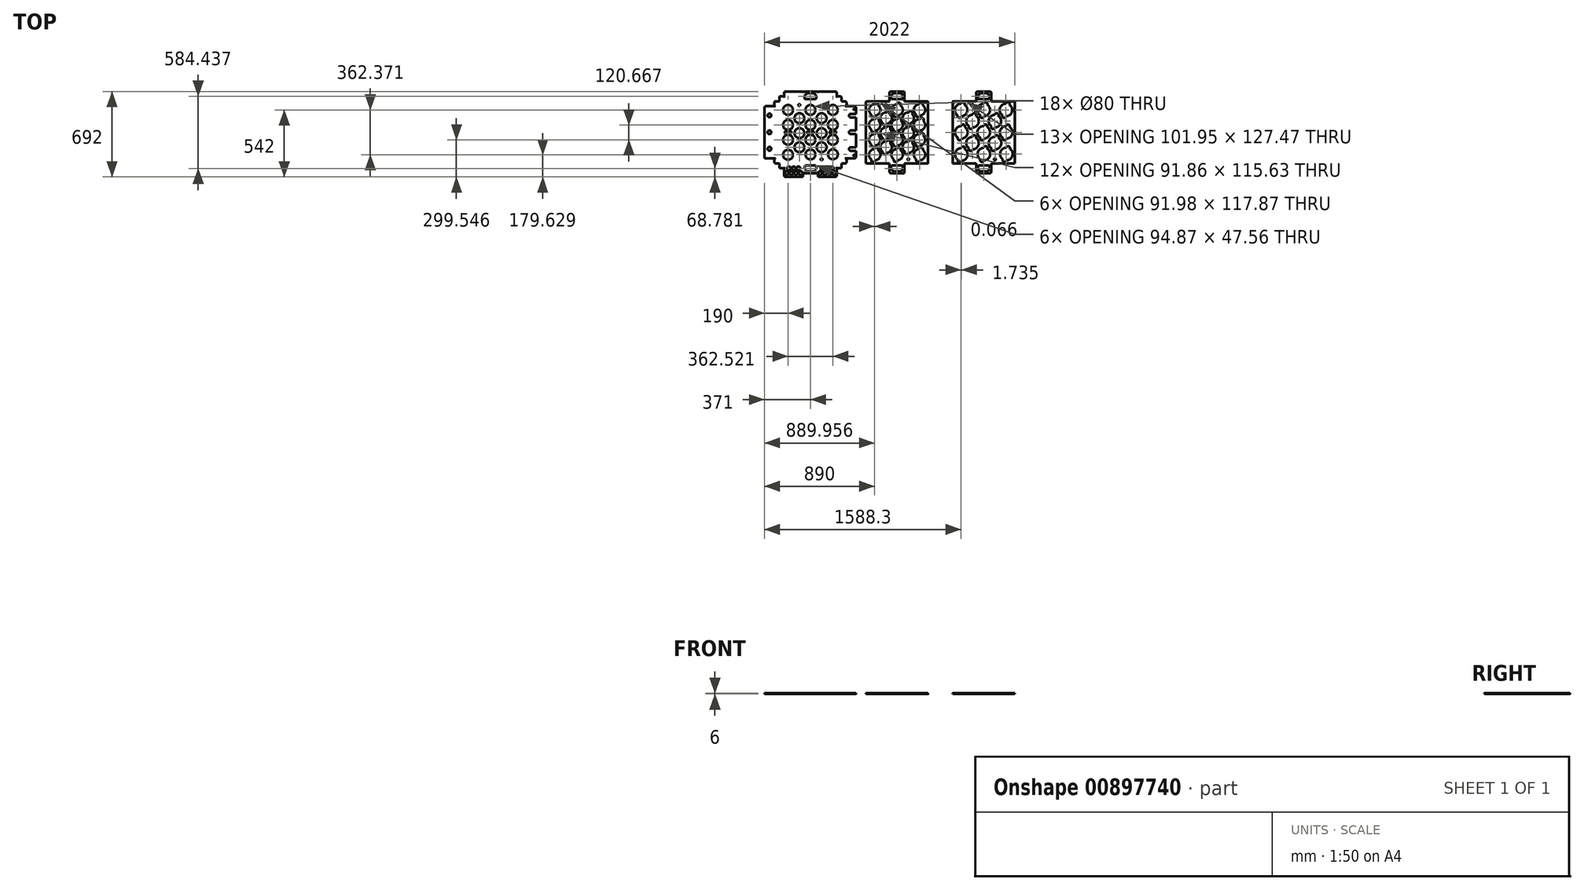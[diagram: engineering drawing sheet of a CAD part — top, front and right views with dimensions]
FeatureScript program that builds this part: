
annotation { "Feature Type Name" : "Feature", "Feature Type Description" : "" }
export const myFeature = defineFeature(function(context is Context, id is Id, definition is map)
    precondition{}
    {
        {
            var Q0;
            Q0=qCreatedBy(makeId("Top.planeOp"),FACE);
            var sketch = newSketch(context, id + "F0", { "sketchPlane" : qUnion([Q0])});
            skLineSegment(sketch, "E0", {"start": v(0, 0) * mm, "end": v(0, -30) * mm});
            skLineSegment(sketch, "E1", {"start": v(10, -40) * mm, "end": v(30, -40) * mm});
            skLineSegment(sketch, "E2", {"start": v(40, -70) * mm, "end": v(40, 0) * mm});
            skLineSegment(sketch, "E3", {"start": v(462.87, 0) * mm, "end": v(462.87, -30) * mm});
            skLineSegment(sketch, "E4", {"start": v(472.87, -40) * mm, "end": v(492, -40) * mm});
            skLineSegment(sketch, "E5", {"start": v(502, -30) * mm, "end": v(502, 0) * mm});
            skLineSegment(sketch, "E6", {"start": v(502, 0) * mm, "end": v(532, 0) * mm});
            skLineSegment(sketch, "E7", {"start": v(542, 10) * mm, "end": v(542, 30) * mm});
            skLineSegment(sketch, "E8", {"start": v(532, 40) * mm, "end": v(502, 40) * mm});
            skLineSegment(sketch, "E9", {"start": v(0, 0) * mm, "end": v(-30, 0) * mm});
            skLineSegment(sketch, "E10", {"start": v(-40, 10) * mm, "end": v(-40, 30) * mm});
            skLineSegment(sketch, "E11", {"start": v(-110, 40) * mm, "end": v(0, 40) * mm});
            skLineSegment(sketch, "E12", {"start": v(-120, 50) * mm, "end": v(-120, 251) * mm});
            skLineSegment(sketch, "E13", {"start": v(-120, 251) * mm, "end": v(45, 251) * mm, "construction": true});
            skLineSegment(sketch, "E14", {"start": v(618, 236) * mm, "end": v(618, 131) * mm});
            skLineSegment(sketch, "E15", {"start": v(251, -80) * mm, "end": v(301, -80) * mm});
            skLineSegment(sketch, "E16.MirrorCS", {"start": v(251, -80) * mm, "end": v(201, -80) * mm});
            skLineSegment(sketch, "E17.MirrorCS", {"start": v(191, -69.74) * mm, "end": v(191, 0) * mm});
            skLineSegment(sketch, "E18.0", {"start": v(298.44, -35) * mm, "end": v(298.44, -27.44) * mm});
            skLineSegment(sketch, "E18.3", {"start": v(203.56, -35) * mm, "end": v(203.56, -27.44) * mm});
            skLineSegment(sketch, "E19.0", {"start": v(213.56, -17.44) * mm, "end": v(288.44, -17.44) * mm});
            skLineSegment(sketch, "E20.0", {"start": v(268.44, -65) * mm, "end": v(233.56, -65) * mm});
            skPoint(sketch, "E21.visualSharp", {"position": v(203.56, -17.44) * mm});
            skPoint(sketch, "E22.visualSharp", {"position": v(298.44, -17.44) * mm});
            skArc(sketch, "E22.filletArc", {"start": v(298.44, -27.44) * mm, "mid": v(295.5, -20.37) * mm, "end": v(288.44, -17.44) * mm});
            skPoint(sketch, "E23.visualSharp", {"position": v(298.44, -65) * mm});
            skPoint(sketch, "E24.visualSharp", {"position": v(203.56, -65) * mm});
            skArc(sketch, "E25.filletArc", {"start": v(213.56, -17.44) * mm, "mid": v(206.5, -20.37) * mm, "end": v(203.56, -27.44) * mm});
            skPoint(sketch, "E26.visualSharp", {"position": v(311, -80) * mm});
            skArc(sketch, "E26.filletArc", {"start": v(301, -80) * mm, "mid": v(308.07, -77.07) * mm, "end": v(311, -70) * mm});
            skPoint(sketch, "E27.visualSharp", {"position": v(191, -80) * mm});
            skArc(sketch, "E27.filletArc", {"start": v(191, -70) * mm, "mid": v(193.93, -77.07) * mm, "end": v(201, -80) * mm});
            skPoint(sketch, "E28.visualSharp", {"position": v(191, 0) * mm});
            skPoint(sketch, "E29.visualSharp", {"position": v(311, 0) * mm});
            skPoint(sketch, "E30.visualSharp", {"position": v(-120, 50) * mm});
            skPoint(sketch, "E31.visualSharp", {"position": v(542, 0) * mm});
            skArc(sketch, "E31.filletArc", {"start": v(532, 0) * mm, "mid": v(539.07, 2.93) * mm, "end": v(542, 10) * mm});
            skPoint(sketch, "E32.visualSharp", {"position": v(542, 40) * mm});
            skArc(sketch, "E32.filletArc", {"start": v(542, 30) * mm, "mid": v(539.07, 37.07) * mm, "end": v(532, 40) * mm});
            skPoint(sketch, "E33.visualSharp", {"position": v(462.87, -40) * mm});
            skArc(sketch, "E33.filletArc", {"start": v(462.87, -30) * mm, "mid": v(465.8, -37.07) * mm, "end": v(472.87, -40) * mm});
            skPoint(sketch, "E34.visualSharp", {"position": v(502, -40) * mm});
            skArc(sketch, "E34.filletArc", {"start": v(492, -40) * mm, "mid": v(499.07, -37.07) * mm, "end": v(502, -30) * mm});
            skPoint(sketch, "E35.visualSharp", {"position": v(40, -40) * mm});
            skArc(sketch, "E35.filletArc", {"start": v(30, -40) * mm, "mid": v(37.07, -37.07) * mm, "end": v(40, -30) * mm});
            skPoint(sketch, "E36.visualSharp", {"position": v(0, -40) * mm});
            skArc(sketch, "E36.filletArc", {"start": v(0, -30) * mm, "mid": v(2.93, -37.07) * mm, "end": v(10, -40) * mm});
            skPoint(sketch, "E37.visualSharp", {"position": v(-40, 0) * mm});
            skArc(sketch, "E37.filletArc", {"start": v(-40, 10) * mm, "mid": v(-37.07, 2.93) * mm, "end": v(-30, 0) * mm});
            skPoint(sketch, "E38.visualSharp", {"position": v(-40, 40) * mm});
            skArc(sketch, "E38.filletArc", {"start": v(-30, 40) * mm, "mid": v(-37.07, 37.07) * mm, "end": v(-40, 30) * mm});
            skArc(sketch, "E39.MirrorCS", {"start": v(301, 582) * mm, "mid": v(308.07, 579.07) * mm, "end": v(311, 572) * mm});
            skArc(sketch, "E40.MirrorCS", {"start": v(492, 542) * mm, "mid": v(499.07, 539.07) * mm, "end": v(502, 532) * mm});
            skLineSegment(sketch, "E41.MirrorCS", {"start": v(472.87, 542) * mm, "end": v(492, 542) * mm});
            skArc(sketch, "E42.MirrorCS", {"start": v(191, 572) * mm, "mid": v(193.93, 579.07) * mm, "end": v(201, 582) * mm});
            skArc(sketch, "E43.MirrorCS", {"start": v(213.56, 519.44) * mm, "mid": v(206.5, 522.37) * mm, "end": v(203.56, 529.44) * mm});
            skArc(sketch, "E44.MirrorCS", {"start": v(542, 472) * mm, "mid": v(539.07, 464.93) * mm, "end": v(532, 462) * mm});
            skLineSegment(sketch, "E45.MirrorCS", {"start": v(203.56, 537) * mm, "end": v(203.56, 529.44) * mm});
            skArc(sketch, "E46.MirrorCS", {"start": v(462.87, 532) * mm, "mid": v(465.8, 539.07) * mm, "end": v(472.87, 542) * mm});
            skLineSegment(sketch, "E47.MirrorCS", {"start": v(-40, 492) * mm, "end": v(-40, 472) * mm});
            skLineSegment(sketch, "E48.MirrorCS", {"start": v(542, 492) * mm, "end": v(542, 472) * mm});
            skLineSegment(sketch, "E49.MirrorCS", {"start": v(298.44, 537) * mm, "end": v(298.44, 529.44) * mm});
            skLineSegment(sketch, "E50.MirrorCS", {"start": v(311, 552) * mm, "end": v(311, 502) * mm});
            skArc(sketch, "E51.MirrorCS", {"start": v(-40, 492) * mm, "mid": v(-37.07, 499.07) * mm, "end": v(-30, 502) * mm});
            skArc(sketch, "E52.MirrorCS", {"start": v(0, 532) * mm, "mid": v(2.93, 539.07) * mm, "end": v(10, 542) * mm});
            skLineSegment(sketch, "E53.MirrorCS", {"start": v(502, 502) * mm, "end": v(532, 502) * mm});
            skLineSegment(sketch, "E54.MirrorCS", {"start": v(10, 542) * mm, "end": v(30, 542) * mm});
            skArc(sketch, "E55.MirrorCS", {"start": v(298.44, 529.44) * mm, "mid": v(295.5, 522.37) * mm, "end": v(288.44, 519.44) * mm});
            skLineSegment(sketch, "E56.MirrorCS", {"start": v(-30, 462) * mm, "end": v(0, 462) * mm});
            skArc(sketch, "E57.MirrorCS", {"start": v(30, 542) * mm, "mid": v(37.07, 539.07) * mm, "end": v(40, 532) * mm});
            skArc(sketch, "E58.MirrorCS", {"start": v(532, 502) * mm, "mid": v(539.07, 499.07) * mm, "end": v(542, 492) * mm});
            skArc(sketch, "E59.MirrorCS", {"start": v(-30, 462) * mm, "mid": v(-37.07, 464.93) * mm, "end": v(-40, 472) * mm});
            skLineSegment(sketch, "E60.MirrorCS", {"start": v(532, 462) * mm, "end": v(502, 462) * mm});
            skLineSegment(sketch, "E61.MirrorCS", {"start": v(268.44, 567) * mm, "end": v(233.56, 567) * mm});
            skLineSegment(sketch, "E62.MirrorCS", {"start": v(462.87, 502) * mm, "end": v(462.87, 532) * mm});
            skLineSegment(sketch, "E63.MirrorCS", {"start": v(502, 532) * mm, "end": v(502, 502) * mm});
            skLineSegment(sketch, "E64.MirrorCS", {"start": v(0, 502) * mm, "end": v(-30, 502) * mm});
            skLineSegment(sketch, "E65.MirrorCS", {"start": v(251, 582) * mm, "end": v(201, 582) * mm});
            skLineSegment(sketch, "E66.MirrorCS", {"start": v(0, 502) * mm, "end": v(0, 532) * mm});
            skLineSegment(sketch, "E67.MirrorCS", {"start": v(40, 532) * mm, "end": v(40, 502) * mm});
            skLineSegment(sketch, "E68.MirrorCS", {"start": v(251, 582) * mm, "end": v(301, 582) * mm});
            skLineSegment(sketch, "E69.MirrorCS", {"start": v(213.56, 519.44) * mm, "end": v(288.44, 519.44) * mm});
            skPoint(sketch, "E70.MirrorP", {"position": v(203.56, 519.44) * mm});
            skPoint(sketch, "E71.MirrorP", {"position": v(0, 542) * mm});
            skPoint(sketch, "E72.MirrorP", {"position": v(40, 542) * mm});
            skPoint(sketch, "E73.MirrorP", {"position": v(542, 502) * mm});
            skPoint(sketch, "E74.MirrorP", {"position": v(298.44, 519.44) * mm});
            skPoint(sketch, "E75.MirrorP", {"position": v(311, 582) * mm});
            skPoint(sketch, "E76.MirrorP", {"position": v(502, 542) * mm});
            skPoint(sketch, "E77.MirrorP", {"position": v(191, 582) * mm});
            skPoint(sketch, "E78.MirrorP", {"position": v(462.87, 542) * mm});
            skPoint(sketch, "E79.MirrorP", {"position": v(-40, 462) * mm});
            skLineSegment(sketch, "E80.MirrorCS", {"start": v(-120, 452) * mm, "end": v(-120, 251) * mm});
            skPoint(sketch, "E81.MirrorP", {"position": v(-40, 502) * mm});
            skPoint(sketch, "E82.MirrorP", {"position": v(618, 452) * mm});
            skLineSegment(sketch, "E83.MirrorCS", {"start": v(618, 266) * mm, "end": v(618, 371) * mm});
            skLineSegment(sketch, "E84.0", {"start": v(-80, 442) * mm, "end": v(-80, 62.82) * mm, "construction": true});
            skLineSegment(sketch, "E85.0", {"start": v(578, 60.47) * mm, "end": v(578, 442) * mm, "construction": true});
            skCircle(sketch, "E86", {"center": v(-80, 251) * mm, "radius": 15 * mm});
            skPoint(sketch, "E86.centerSnap0", {"position": v(-80, 252.4) * mm});
            skArc(sketch, "E87", {"start": v(578, 266) * mm, "mid": v(563, 251) * mm, "end": v(578, 236) * mm});
            skArc(sketch, "E88", {"start": v(578, 401) * mm, "mid": v(563, 386) * mm, "end": v(578, 371) * mm});
            skArc(sketch, "E89", {"start": v(578, 131) * mm, "mid": v(563, 116) * mm, "end": v(578, 101) * mm});
            skCircle(sketch, "E90", {"center": v(-80, 387.4) * mm, "radius": 15 * mm});
            skCircle(sketch, "E91", {"center": v(-80, 117.4) * mm, "radius": 15 * mm});
            skLineSegment(sketch, "E92", {"start": v(578, 401) * mm, "end": v(618, 401) * mm});
            skLineSegment(sketch, "E93", {"start": v(578, 371) * mm, "end": v(618, 371) * mm});
            skLineSegment(sketch, "E94", {"start": v(578, 266) * mm, "end": v(618, 266) * mm});
            skLineSegment(sketch, "E95", {"start": v(578, 236) * mm, "end": v(618, 236) * mm});
            skLineSegment(sketch, "E96", {"start": v(578, 131) * mm, "end": v(618, 131) * mm});
            skLineSegment(sketch, "E97", {"start": v(578, 101) * mm, "end": v(618, 101) * mm});
            skLineSegment(sketch, "E98.trimOffspring", {"start": v(618, 401) * mm, "end": v(618, 452) * mm});
            skPoint(sketch, "E99.orphan", {"position": v(618, 251) * mm});
            skLineSegment(sketch, "E100.trimOffspring", {"start": v(618, 101) * mm, "end": v(618, 50) * mm});
            skLineSegment(sketch, "E101", {"start": v(50, 582) * mm, "end": v(181, 582) * mm});
            skPoint(sketch, "E102.visualSharp", {"position": v(170, 582) * mm});
            skLineSegment(sketch, "E103", {"start": v(452.87, 582) * mm, "end": v(321, 582) * mm});
            skLineSegment(sketch, "E104", {"start": v(191, 572) * mm, "end": v(191, 502) * mm});
            skLineSegment(sketch, "E105.0", {"start": v(432, 432) * mm, "end": v(69.97, 432) * mm, "construction": true});
            skLineSegment(sketch, "E106.0", {"start": v(432, 432) * mm, "end": v(70, 432) * mm, "construction": true});
            skLineSegment(sketch, "E107", {"start": v(70, 65) * mm, "end": v(70, 432) * mm, "construction": true});
            skLineSegment(sketch, "E108.0", {"start": v(432, 311.33) * mm, "end": v(70, 311.33) * mm, "construction": true});
            skLineSegment(sketch, "E109.0", {"start": v(432, 190.67) * mm, "end": v(70, 190.67) * mm, "construction": true});
            skLineSegment(sketch, "E110", {"start": v(251, 432) * mm, "end": v(251, 70) * mm, "construction": true});
            skCircle(sketch, "E111", {"center": v(70, 432) * mm, "radius": 40 * mm});
            skCircle(sketch, "E112", {"center": v(251, 432) * mm, "radius": 40 * mm});
            skCircle(sketch, "E113", {"center": v(432, 432) * mm, "radius": 40 * mm});
            skCircle(sketch, "E114", {"center": v(341.53, 365.69) * mm, "radius": 40 * mm});
            skCircle(sketch, "E115", {"center": v(70.07, 69.63) * mm, "radius": 40 * mm});
            skCircle(sketch, "E116", {"center": v(251, 72.13) * mm, "radius": 40 * mm});
            skCircle(sketch, "E117", {"center": v(341.53, 245.02) * mm, "radius": 40 * mm});
            skCircle(sketch, "E118", {"center": v(341.5, 130.33) * mm, "radius": 40 * mm});
            skCircle(sketch, "E119", {"center": v(432.52, 72.87) * mm, "radius": 40 * mm});
            skLineSegment(sketch, "E120", {"start": v(251, 65) * mm, "end": v(251, 427) * mm, "construction": true});
            skLineSegment(sketch, "E121.trimOffspring", {"start": v(95, 246) * mm, "end": v(95, 256) * mm});
            skLineSegment(sketch, "E122.trimOffspring", {"start": v(226, 246) * mm, "end": v(226, 256) * mm});
            skLineSegment(sketch, "E123.trimOffspring", {"start": v(276, 246) * mm, "end": v(276, 256) * mm});
            skLineSegment(sketch, "E124.trimOffspring", {"start": v(457.52, 246) * mm, "end": v(457.52, 256) * mm});
            skLineSegment(sketch, "E125.trimOffspring", {"start": v(407.52, 246) * mm, "end": v(407.52, 256) * mm});
            skArc(sketch, "E126.trimOffspring", {"start": v(432.52, 230.66) * mm, "mid": v(432.26, 230.67) * mm, "end": v(432, 230.67) * mm});
            skArc(sketch, "E127.trimOffspring", {"start": v(432, 271.33) * mm, "mid": v(432.26, 271.33) * mm, "end": v(432.52, 271.34) * mm});
            skLineSegment(sketch, "E128", {"start": v(70.07, 69.63) * mm, "end": v(70.02, 230.67) * mm, "construction": true});
            skLineSegment(sketch, "E129", {"start": v(432, 432) * mm, "end": v(432.52, 70.74) * mm, "construction": true});
            skLineSegment(sketch, "E130", {"start": v(341.5, 130.33) * mm, "end": v(341.53, 365.69) * mm, "construction": true});
            skLineSegment(sketch, "E131", {"start": v(69.99, 365.69) * mm, "end": v(251, 365.69) * mm, "construction": true});
            skLineSegment(sketch, "E132", {"start": v(162.1, 130.33) * mm, "end": v(162.13, 365.69) * mm, "construction": true});
            skCircle(sketch, "E133", {"center": v(162.13, 365.69) * mm, "radius": 40 * mm});
            skCircle(sketch, "E134", {"center": v(162.13, 245.02) * mm, "radius": 40 * mm});
            skCircle(sketch, "E135", {"center": v(162.1, 130.33) * mm, "radius": 40 * mm});
            skCircle(sketch, "E136.converted", {"center": v(432, 311.33) * mm, "radius": 40 * mm});
            skCircle(sketch, "E137.converted", {"center": v(251, 311.33) * mm, "radius": 40 * mm});
            skCircle(sketch, "E138.converted", {"center": v(70, 190.67) * mm, "radius": 40 * mm});
            skCircle(sketch, "E139.converted", {"center": v(251, 190.67) * mm, "radius": 40 * mm});
            skCircle(sketch, "E140.converted", {"center": v(432, 190.67) * mm, "radius": 40 * mm});
            skLineSegment(sketch, "E141", {"start": v(90, 261) * mm, "end": v(50, 261) * mm});
            skLineSegment(sketch, "E142", {"start": v(45, 256) * mm, "end": v(45, 246) * mm});
            skLineSegment(sketch, "E143", {"start": v(50, 241) * mm, "end": v(90, 241) * mm});
            skCircle(sketch, "E144.converted", {"center": v(70, 311.33) * mm, "radius": 40 * mm});
            skPoint(sketch, "E145.orphan", {"position": v(95, 280.1) * mm});
            skPoint(sketch, "E146.orphan", {"position": v(95, 221.9) * mm});
            skPoint(sketch, "E147.orphan", {"position": v(45, 221.9) * mm});
            skPoint(sketch, "E148.orphan", {"position": v(45, 280.1) * mm});
            skLineSegment(sketch, "E149.trimOffspring", {"start": v(95, 251) * mm, "end": v(563, 251) * mm, "construction": true});
            skLineSegment(sketch, "E150.trimOffspring", {"start": v(70, 251) * mm, "end": v(70.02, 251) * mm});
            skArc(sketch, "E151.filletArc", {"start": v(95, 256) * mm, "mid": v(93.54, 259.54) * mm, "end": v(90, 261) * mm});
            skArc(sketch, "E152.filletArc", {"start": v(90, 241) * mm, "mid": v(93.54, 242.46) * mm, "end": v(95, 246) * mm});
            skArc(sketch, "E153.filletArc", {"start": v(50, 261) * mm, "mid": v(46.46, 259.54) * mm, "end": v(45, 256) * mm});
            skArc(sketch, "E154.filletArc", {"start": v(45, 246) * mm, "mid": v(46.46, 242.46) * mm, "end": v(50, 241) * mm});
            skLineSegment(sketch, "E155", {"start": v(271, 261) * mm, "end": v(231, 261) * mm});
            skLineSegment(sketch, "E156", {"start": v(226, 256) * mm, "end": v(226, 246) * mm});
            skLineSegment(sketch, "E157", {"start": v(231, 241) * mm, "end": v(271, 241) * mm});
            skLineSegment(sketch, "E158.trimOffspring", {"start": v(251, 251) * mm, "end": v(251.02, 251) * mm});
            skArc(sketch, "E159.filletArc", {"start": v(276, 256) * mm, "mid": v(274.54, 259.54) * mm, "end": v(271, 261) * mm});
            skArc(sketch, "E160.filletArc", {"start": v(271, 241) * mm, "mid": v(274.54, 242.46) * mm, "end": v(276, 246) * mm});
            skArc(sketch, "E161.filletArc", {"start": v(231, 261) * mm, "mid": v(227.46, 259.54) * mm, "end": v(226, 256) * mm});
            skArc(sketch, "E162.filletArc", {"start": v(226, 246) * mm, "mid": v(227.46, 242.46) * mm, "end": v(231, 241) * mm});
            skLineSegment(sketch, "E163", {"start": v(452.52, 261) * mm, "end": v(412.52, 261) * mm});
            skLineSegment(sketch, "E164", {"start": v(407.52, 256) * mm, "end": v(407.52, 246) * mm});
            skLineSegment(sketch, "E165", {"start": v(412.52, 241) * mm, "end": v(452.52, 241) * mm});
            skLineSegment(sketch, "E166.trimOffspring", {"start": v(432.52, 251) * mm, "end": v(432.54, 251) * mm});
            skArc(sketch, "E167.filletArc", {"start": v(457.52, 256) * mm, "mid": v(456.06, 259.54) * mm, "end": v(452.52, 261) * mm});
            skArc(sketch, "E168.filletArc", {"start": v(452.52, 241) * mm, "mid": v(456.06, 242.46) * mm, "end": v(457.52, 246) * mm});
            skArc(sketch, "E169.filletArc", {"start": v(412.52, 261) * mm, "mid": v(408.99, 259.54) * mm, "end": v(407.52, 256) * mm});
            skArc(sketch, "E170.filletArc", {"start": v(407.52, 246) * mm, "mid": v(408.99, 242.46) * mm, "end": v(412.52, 241) * mm});
            skCircle(sketch, "E171", {"center": v(578, 116) * mm, "radius": 15 * mm, "construction": true});
            skLineSegment(sketch, "E172.0", {"start": v(603, 101) * mm, "end": v(603, 50) * mm, "construction": true});
            skCircle(sketch, "E173", {"center": v(603, 65) * mm, "radius": 4.25 * mm});
            skLineSegment(sketch, "E174.0", {"start": v(603, 401) * mm, "end": v(603, 452) * mm, "construction": true});
            skCircle(sketch, "E175", {"center": v(603, 437) * mm, "radius": 4.25 * mm});
            skLineSegment(sketch, "E176", {"start": v(64, 0) * mm, "end": v(164, 0) * mm, "construction": true});
            skLineSegment(sketch, "E177.0", {"start": v(77.75, -40) * mm, "end": v(115.5, -40) * mm, "construction": true});
            skCircle(sketch, "E178", {"center": v(77.75, -40) * mm, "radius": 15 * mm});
            skCircle(sketch, "E179", {"center": v(115.5, -40) * mm, "radius": 15 * mm});
            skCircle(sketch, "E180", {"center": v(153.25, -40) * mm, "radius": 15 * mm});
            skPoint(sketch, "E181.orphan", {"position": v(40, -20) * mm});
            skLineSegment(sketch, "E182", {"start": v(115.5, -40) * mm, "end": v(130.5, -40) * mm, "construction": true});
            skLineSegment(sketch, "E183", {"start": v(77.75, -40) * mm, "end": v(40, -40) * mm, "construction": true});
            skLineSegment(sketch, "E184.0", {"start": v(191, -77.75) * mm, "end": v(40, -77.75) * mm, "construction": true});
            skLineSegment(sketch, "E185", {"start": v(58.87, -40) * mm, "end": v(58.87, -77.75) * mm, "construction": true});
            skLineSegment(sketch, "E186", {"start": v(96.62, -40) * mm, "end": v(96.62, -77.75) * mm, "construction": true});
            skLineSegment(sketch, "E187", {"start": v(153.25, -40) * mm, "end": v(191, -40) * mm, "construction": true});
            skLineSegment(sketch, "E188", {"start": v(172.12, -40) * mm, "end": v(172.12, -77.75) * mm, "construction": true});
            skCircle(sketch, "E189", {"center": v(58.87, -77.75) * mm, "radius": 15 * mm});
            skCircle(sketch, "E190", {"center": v(96.62, -77.75) * mm, "radius": 15 * mm});
            skLineSegment(sketch, "E191", {"start": v(134.37, -40) * mm, "end": v(134.37, -77.75) * mm, "construction": true});
            skCircle(sketch, "E192", {"center": v(134.37, -77.75) * mm, "radius": 15 * mm});
            skCircle(sketch, "E193", {"center": v(172.12, -77.75) * mm, "radius": 15 * mm});
            skPoint(sketch, "E194.visualSharp", {"position": v(462, -80) * mm});
            skPoint(sketch, "E195.visualSharp", {"position": v(462, 0) * mm});
            skLineSegment(sketch, "E196.0", {"start": v(348.75, -40) * mm, "end": v(386.5, -40) * mm, "construction": true});
            skCircle(sketch, "E197", {"center": v(348.75, -40) * mm, "radius": 15 * mm});
            skCircle(sketch, "E198", {"center": v(386.5, -40) * mm, "radius": 15 * mm});
            skCircle(sketch, "E199", {"center": v(424.25, -40) * mm, "radius": 15 * mm});
            skLineSegment(sketch, "E200.trimOffspring", {"start": v(401.5, -40) * mm, "end": v(409.25, -40) * mm, "construction": true});
            skLineSegment(sketch, "E201", {"start": v(386.5, -40) * mm, "end": v(401.5, -40) * mm, "construction": true});
            skLineSegment(sketch, "E202", {"start": v(348.75, -40) * mm, "end": v(311, -40) * mm, "construction": true});
            skLineSegment(sketch, "E203.0", {"start": v(462, -77.75) * mm, "end": v(311, -77.75) * mm, "construction": true});
            skLineSegment(sketch, "E204", {"start": v(329.87, -40) * mm, "end": v(329.87, -77.75) * mm, "construction": true});
            skLineSegment(sketch, "E205", {"start": v(367.62, -40) * mm, "end": v(367.62, -77.75) * mm, "construction": true});
            skLineSegment(sketch, "E206", {"start": v(424.25, -40) * mm, "end": v(462, -40) * mm, "construction": true});
            skLineSegment(sketch, "E207", {"start": v(443.12, -40) * mm, "end": v(443.12, -77.75) * mm, "construction": true});
            skCircle(sketch, "E208", {"center": v(329.87, -77.75) * mm, "radius": 15 * mm});
            skCircle(sketch, "E209", {"center": v(367.62, -77.75) * mm, "radius": 15 * mm});
            skLineSegment(sketch, "E210", {"start": v(405.37, -40) * mm, "end": v(405.37, -77.75) * mm, "construction": true});
            skCircle(sketch, "E211", {"center": v(405.37, -77.75) * mm, "radius": 15 * mm});
            skCircle(sketch, "E212", {"center": v(443.12, -77.75) * mm, "radius": 15 * mm});
            skLineSegment(sketch, "E213", {"start": v(191, -69.74) * mm, "end": v(191, -70) * mm});
            skPoint(sketch, "E214.visualSharp", {"position": v(40, -80) * mm});
            skLineSegment(sketch, "E215.0", {"start": v(181, -110) * mm, "end": v(50, -110) * mm});
            skLineSegment(sketch, "E216.0", {"start": v(452.89, -109.73) * mm, "end": v(321.02, -109.98) * mm});
            skPoint(sketch, "E217.newPointA", {"position": v(203.56, -55) * mm});
            skPoint(sketch, "E217.newPointB", {"position": v(213.56, -65) * mm});
            skArc(sketch, "E217.filletArc", {"start": v(203.56, -35) * mm, "mid": v(212.35, -56.21) * mm, "end": v(233.56, -65) * mm});
            skPoint(sketch, "E218.newPointA", {"position": v(288.44, -65) * mm});
            skPoint(sketch, "E218.newPointB", {"position": v(298.44, -55) * mm});
            skArc(sketch, "E218.filletArc", {"start": v(268.44, -65) * mm, "mid": v(289.65, -56.21) * mm, "end": v(298.44, -35) * mm});
            skLineSegment(sketch, "E219", {"start": v(462.87, -30) * mm, "end": v(462.87, -99.73) * mm});
            skLineSegment(sketch, "E220", {"start": v(311, 0) * mm, "end": v(311, -99.98) * mm});
            skLineSegment(sketch, "E221", {"start": v(191, -69.74) * mm, "end": v(191, -100) * mm});
            skLineSegment(sketch, "E222", {"start": v(40, -70) * mm, "end": v(40, -100) * mm});
            skArc(sketch, "E223.filletArc", {"start": v(452.89, -109.73) * mm, "mid": v(459.95, -106.8) * mm, "end": v(462.87, -99.73) * mm});
            skPoint(sketch, "E224.visualSharp", {"position": v(311, -110) * mm});
            skArc(sketch, "E224.filletArc", {"start": v(311, -99.98) * mm, "mid": v(313.94, -107.06) * mm, "end": v(321.02, -109.98) * mm});
            skArc(sketch, "E225.filletArc", {"start": v(181, -110) * mm, "mid": v(188.07, -107.07) * mm, "end": v(191, -100) * mm});
            skArc(sketch, "E226.filletArc", {"start": v(40, -100) * mm, "mid": v(42.93, -107.07) * mm, "end": v(50, -110) * mm});
            skArc(sketch, "E227.filletArc", {"start": v(233.56, 567) * mm, "mid": v(212.35, 558.21) * mm, "end": v(203.56, 537) * mm});
            skArc(sketch, "E228.filletArc", {"start": v(298.44, 537) * mm, "mid": v(289.65, 558.21) * mm, "end": v(268.44, 567) * mm});
            skPoint(sketch, "E229.newPointA", {"position": v(311, 572) * mm});
            skLineSegment(sketch, "E230", {"start": v(311, 552) * mm, "end": v(311, 572) * mm});
            skArc(sketch, "E231.filletArc", {"start": v(321, 582) * mm, "mid": v(313.93, 579.07) * mm, "end": v(311, 572) * mm});
            skArc(sketch, "E232.filletArc", {"start": v(191, 572) * mm, "mid": v(188.07, 579.07) * mm, "end": v(181, 582) * mm});
            skLineSegment(sketch, "E233", {"start": v(70, 472) * mm, "end": v(251, 472) * mm, "construction": true});
            skCircle(sketch, "E234", {"center": v(160.5, 472) * mm, "radius": 7.5 * mm});
            skLineSegment(sketch, "E235", {"start": v(432, 32.87) * mm, "end": v(251, 32.13) * mm, "construction": true});
            skCircle(sketch, "E236", {"center": v(341.5, 32.5) * mm, "radius": 7.5 * mm});
            skPoint(sketch, "E237.orphan", {"position": v(-120, 60) * mm});
            skArc(sketch, "E238.filletArc", {"start": v(-120, 50) * mm, "mid": v(-117.07, 42.93) * mm, "end": v(-110, 40) * mm});
            skPoint(sketch, "E239.end.orphan", {"position": v(0, 50) * mm});
            skLineSegment(sketch, "E240", {"start": v(-30, 462) * mm, "end": v(-110, 462) * mm});
            skPoint(sketch, "E241.orphan", {"position": v(-120, 442) * mm});
            skArc(sketch, "E242.filletArc", {"start": v(-110, 462) * mm, "mid": v(-117.07, 459.07) * mm, "end": v(-120, 452) * mm});
            skLineSegment(sketch, "E243", {"start": v(40, 532) * mm, "end": v(40, 572) * mm});
            skPoint(sketch, "E244.orphan", {"position": v(70, 582) * mm});
            skPoint(sketch, "E245.visualSharp", {"position": v(40, 582) * mm});
            skArc(sketch, "E245.filletArc", {"start": v(50, 582) * mm, "mid": v(42.93, 579.07) * mm, "end": v(40, 572) * mm});
            skLineSegment(sketch, "E246", {"start": v(462.87, 532) * mm, "end": v(462.87, 572) * mm});
            skPoint(sketch, "E247.orphan", {"position": v(432.87, 582) * mm});
            skPoint(sketch, "E248.visualSharp", {"position": v(462.87, 582) * mm});
            skArc(sketch, "E248.filletArc", {"start": v(462.87, 572) * mm, "mid": v(459.94, 579.07) * mm, "end": v(452.87, 582) * mm});
            skLineSegment(sketch, "E249", {"start": v(532, 462) * mm, "end": v(608, 462) * mm});
            skPoint(sketch, "E250.orphan", {"position": v(618, 442) * mm});
            skPoint(sketch, "E251.visualSharp", {"position": v(618, 462) * mm});
            skArc(sketch, "E251.filletArc", {"start": v(618, 452) * mm, "mid": v(615.07, 459.07) * mm, "end": v(608, 462) * mm});
            skLineSegment(sketch, "E252", {"start": v(532, 40) * mm, "end": v(608, 40) * mm});
            skPoint(sketch, "E253.orphan", {"position": v(618, 60) * mm});
            skPoint(sketch, "E254.visualSharp", {"position": v(618, 40) * mm});
            skArc(sketch, "E254.filletArc", {"start": v(608, 40) * mm, "mid": v(615.07, 42.93) * mm, "end": v(618, 50) * mm});
            skSolve(sketch);
        }
        {
            var Q0;
            Q0=makeQuery(id+"F0.imprint","IMPRINT",FACE,{"disambiguationData":[TD([[makeQuery(id+"F0.imprint","IMPRINT",EDGE,{"derivedFrom":sQuery(id+"F0.wireOp",EDGE,"f0b15c86-8dd5-4f4f-8183-a0a3af1ac7910.MirrorCS")}),1.0]])]});
            var Q1;
            Q1=makeQuery(id+"F0.imprint","IMPRINT",FACE,{"disambiguationData":[TD([[makeQuery(id+"F0.imprint","IMPRINT",EDGE,{"derivedFrom":sQuery(id+"F0.wireOp",EDGE,"E0")}),1.0]])]});
            var Q2;
            Q2=makeQuery(id+"F0.imprint","IMPRINT",FACE,{"disambiguationData":[TD([[makeQuery(id+"F0.imprint","IMPRINT",EDGE,{"derivedFrom":sQuery(id+"F0.wireOp",EDGE,"E39.MirrorCS")}),-1.0]])]});
            extrude(context, id + "F1", {"entities" : qUnion([Q0, Q1, Q2]), "depth" : 6 * mm, "offsetDistance" : 25 * mm});
        }
        {
            var Q0;
            Q0=qCreatedBy(makeId("Top.planeOp"),FACE);
            var sketch = newSketch(context, id + "F2", { "sketchPlane" : qUnion([Q0])});
            skLineSegment(sketch, "E255", {"start": v(0, 0) * mm, "end": v(700, 0) * mm, "construction": true});
            skLineSegment(sketch, "E256", {"start": v(705, 0) * mm, "end": v(891, 0) * mm, "construction": true});
            skLineSegment(sketch, "E257", {"start": v(700, 0) * mm, "end": v(891, 0) * mm});
            skLineSegment(sketch, "E258", {"start": v(1202, 5) * mm, "end": v(1202, 497) * mm});
            skLineSegment(sketch, "E259", {"start": v(1197, 502) * mm, "end": v(1011, 502) * mm});
            skLineSegment(sketch, "E260", {"start": v(700, 497) * mm, "end": v(700, 5) * mm});
            skLineSegment(sketch, "E261", {"start": v(1902, 5) * mm, "end": v(1902, 497) * mm, "construction": true});
            skArc(sketch, "E262", {"start": v(768.3, 115.6) * mm, "mid": v(725.97, 82.74) * mm, "end": v(743.46, 32.1) * mm});
            skArc(sketch, "E263", {"start": v(796.67, 107.16) * mm, "mid": v(787.46, 128.1) * mm, "end": v(768.3, 115.6) * mm});
            skArc(sketch, "E264", {"start": v(743.46, 32.1) * mm, "mid": v(752.67, 11.16) * mm, "end": v(771.83, 23.66) * mm});
            skArc(sketch, "E265.trimOffspring", {"start": v(771.83, 23.66) * mm, "mid": v(814.16, 56.51) * mm, "end": v(796.67, 107.16) * mm});
            skArc(sketch, "E266", {"start": v(949.23, 477.97) * mm, "mid": v(906.9, 445.11) * mm, "end": v(924.4, 394.47) * mm});
            skArc(sketch, "E267", {"start": v(977.6, 469.53) * mm, "mid": v(968.4, 490.47) * mm, "end": v(949.23, 477.97) * mm});
            skArc(sketch, "E268", {"start": v(924.4, 394.47) * mm, "mid": v(933.6, 373.53) * mm, "end": v(952.77, 386.03) * mm});
            skArc(sketch, "E269.trimOffspring", {"start": v(952.77, 386.03) * mm, "mid": v(995.1, 418.89) * mm, "end": v(977.6, 469.53) * mm});
            skArc(sketch, "E270", {"start": v(949.23, 115.97) * mm, "mid": v(906.9, 83.11) * mm, "end": v(924.4, 32.47) * mm});
            skArc(sketch, "E271", {"start": v(977.6, 107.53) * mm, "mid": v(968.4, 128.47) * mm, "end": v(949.23, 115.97) * mm});
            skArc(sketch, "E272", {"start": v(924.4, 32.47) * mm, "mid": v(933.6, 11.53) * mm, "end": v(952.77, 24.03) * mm});
            skArc(sketch, "E273.trimOffspring", {"start": v(952.77, 24.03) * mm, "mid": v(995.1, 56.89) * mm, "end": v(977.6, 107.53) * mm});
            skArc(sketch, "E274", {"start": v(1130.23, 477.97) * mm, "mid": v(1087.9, 445.11) * mm, "end": v(1105.4, 394.47) * mm});
            skArc(sketch, "E275", {"start": v(1158.6, 469.53) * mm, "mid": v(1149.4, 490.47) * mm, "end": v(1130.23, 477.97) * mm});
            skArc(sketch, "E276", {"start": v(1105.4, 394.47) * mm, "mid": v(1114.6, 373.53) * mm, "end": v(1133.77, 386.03) * mm});
            skArc(sketch, "E277.trimOffspring", {"start": v(1133.77, 386.03) * mm, "mid": v(1176.1, 418.89) * mm, "end": v(1158.6, 469.53) * mm});
            skArc(sketch, "E278", {"start": v(1130.62, 116.7) * mm, "mid": v(1088.43, 83.86) * mm, "end": v(1105.8, 33.3) * mm});
            skArc(sketch, "E279", {"start": v(1159.01, 108.35) * mm, "mid": v(1149.74, 129.26) * mm, "end": v(1130.62, 116.7) * mm});
            skArc(sketch, "E280", {"start": v(1105.8, 33.3) * mm, "mid": v(1114.96, 12.32) * mm, "end": v(1134.15, 24.77) * mm});
            skArc(sketch, "E281.trimOffspring", {"start": v(1134.15, 24.77) * mm, "mid": v(1176.61, 57.63) * mm, "end": v(1159.01, 108.35) * mm});
            skArc(sketch, "E282", {"start": v(774.99, 357.06) * mm, "mid": v(727, 327.65) * mm, "end": v(743.4, 273.8) * mm});
            skArc(sketch, "E283", {"start": v(801.81, 344.56) * mm, "mid": v(795.77, 366.62) * mm, "end": v(774.99, 357.06) * mm});
            skArc(sketch, "E284", {"start": v(743.4, 273.8) * mm, "mid": v(752.6, 252.87) * mm, "end": v(771.77, 265.37) * mm});
            skArc(sketch, "E285.trimOffspring", {"start": v(771.77, 265.37) * mm, "mid": v(813, 295.01) * mm, "end": v(801.81, 344.56) * mm});
            skArc(sketch, "E286", {"start": v(774.99, 236.4) * mm, "mid": v(727, 206.99) * mm, "end": v(743.4, 153.14) * mm});
            skArc(sketch, "E287", {"start": v(801.81, 223.9) * mm, "mid": v(795.77, 245.96) * mm, "end": v(774.99, 236.4) * mm});
            skArc(sketch, "E288", {"start": v(743.4, 153.14) * mm, "mid": v(752.6, 132.2) * mm, "end": v(771.77, 144.7) * mm});
            skArc(sketch, "E289.trimOffspring", {"start": v(771.77, 144.7) * mm, "mid": v(813, 174.35) * mm, "end": v(801.81, 223.9) * mm});
            skArc(sketch, "E290", {"start": v(955.99, 357.06) * mm, "mid": v(908, 327.65) * mm, "end": v(924.4, 273.8) * mm});
            skArc(sketch, "E291", {"start": v(982.81, 344.56) * mm, "mid": v(976.77, 366.62) * mm, "end": v(955.99, 357.06) * mm});
            skArc(sketch, "E292", {"start": v(924.4, 273.8) * mm, "mid": v(933.6, 252.87) * mm, "end": v(952.77, 265.37) * mm});
            skArc(sketch, "E293.trimOffspring", {"start": v(952.77, 265.37) * mm, "mid": v(994, 295.01) * mm, "end": v(982.81, 344.56) * mm});
            skArc(sketch, "E294", {"start": v(955.99, 236.4) * mm, "mid": v(908, 206.99) * mm, "end": v(924.4, 153.14) * mm});
            skArc(sketch, "E295", {"start": v(982.81, 223.9) * mm, "mid": v(976.77, 245.96) * mm, "end": v(955.99, 236.4) * mm});
            skArc(sketch, "E296", {"start": v(924.4, 153.14) * mm, "mid": v(933.6, 132.2) * mm, "end": v(952.77, 144.7) * mm});
            skArc(sketch, "E297.trimOffspring", {"start": v(952.77, 144.7) * mm, "mid": v(994, 174.35) * mm, "end": v(982.81, 223.9) * mm});
            skArc(sketch, "E298", {"start": v(1136.99, 357.06) * mm, "mid": v(1089, 327.65) * mm, "end": v(1105.4, 273.8) * mm});
            skArc(sketch, "E299", {"start": v(1163.81, 344.56) * mm, "mid": v(1157.77, 366.62) * mm, "end": v(1136.99, 357.06) * mm});
            skArc(sketch, "E300", {"start": v(1105.4, 273.8) * mm, "mid": v(1114.6, 252.87) * mm, "end": v(1133.77, 265.37) * mm});
            skArc(sketch, "E301.trimOffspring", {"start": v(1133.77, 265.37) * mm, "mid": v(1175, 295.01) * mm, "end": v(1163.81, 344.56) * mm});
            skArc(sketch, "E302", {"start": v(1136.99, 236.4) * mm, "mid": v(1089, 206.99) * mm, "end": v(1105.4, 153.14) * mm});
            skArc(sketch, "E303", {"start": v(1163.81, 223.9) * mm, "mid": v(1157.77, 245.96) * mm, "end": v(1136.99, 236.4) * mm});
            skArc(sketch, "E304", {"start": v(1105.4, 153.14) * mm, "mid": v(1114.6, 132.2) * mm, "end": v(1133.77, 144.7) * mm});
            skArc(sketch, "E305.trimOffspring", {"start": v(1133.77, 144.7) * mm, "mid": v(1175, 174.35) * mm, "end": v(1163.81, 223.9) * mm});
            skArc(sketch, "E306", {"start": v(1046.52, 411.42) * mm, "mid": v(998.52, 382) * mm, "end": v(1014.93, 328.16) * mm});
            skArc(sketch, "E307", {"start": v(1073.35, 398.91) * mm, "mid": v(1067.3, 420.98) * mm, "end": v(1046.52, 411.42) * mm});
            skArc(sketch, "E308", {"start": v(1014.93, 328.16) * mm, "mid": v(1024.14, 307.22) * mm, "end": v(1043.3, 319.72) * mm});
            skArc(sketch, "E309.trimOffspring", {"start": v(1043.3, 319.72) * mm, "mid": v(1084.54, 349.37) * mm, "end": v(1073.35, 398.91) * mm});
            skArc(sketch, "E310", {"start": v(1046.52, 290.75) * mm, "mid": v(998.52, 261.34) * mm, "end": v(1014.93, 207.5) * mm});
            skArc(sketch, "E311", {"start": v(1073.35, 278.25) * mm, "mid": v(1067.3, 300.3) * mm, "end": v(1046.52, 290.75) * mm});
            skArc(sketch, "E312", {"start": v(1014.93, 207.5) * mm, "mid": v(1024.14, 186.55) * mm, "end": v(1043.3, 199.06) * mm});
            skArc(sketch, "E313.trimOffspring", {"start": v(1043.3, 199.06) * mm, "mid": v(1084.54, 228.7) * mm, "end": v(1073.35, 278.25) * mm});
            skArc(sketch, "E314", {"start": v(1046.49, 176.06) * mm, "mid": v(998.5, 146.65) * mm, "end": v(1014.9, 92.8) * mm});
            skArc(sketch, "E315", {"start": v(1073.31, 163.56) * mm, "mid": v(1067.27, 185.62) * mm, "end": v(1046.49, 176.06) * mm});
            skArc(sketch, "E316", {"start": v(1014.9, 92.8) * mm, "mid": v(1024.1, 71.87) * mm, "end": v(1043.27, 84.37) * mm});
            skArc(sketch, "E317.trimOffspring", {"start": v(1043.27, 84.37) * mm, "mid": v(1084.5, 114.01) * mm, "end": v(1073.31, 163.56) * mm});
            skLineSegment(sketch, "E318", {"start": v(1902, 0) * mm, "end": v(1902, 502) * mm});
            skLineSegment(sketch, "E319", {"start": v(1400, 497) * mm, "end": v(1400, 5) * mm});
            skArc(sketch, "E320", {"start": v(1652.12, 125.8) * mm, "mid": v(1603.54, 89.33) * mm, "end": v(1624.3, 32.25) * mm});
            skArc(sketch, "E321", {"start": v(1680.56, 117.33) * mm, "mid": v(1671.24, 138.05) * mm, "end": v(1652.12, 125.8) * mm});
            skArc(sketch, "E322", {"start": v(1624.3, 32.25) * mm, "mid": v(1633.6, 11.53) * mm, "end": v(1652.74, 23.8) * mm});
            skArc(sketch, "E323.trimOffspring", {"start": v(1652.74, 23.8) * mm, "mid": v(1701.3, 60.25) * mm, "end": v(1680.56, 117.33) * mm});
            skArc(sketch, "E324", {"start": v(1833.5, 126.53) * mm, "mid": v(1785.08, 90.07) * mm, "end": v(1805.7, 33.07) * mm});
            skArc(sketch, "E325", {"start": v(1861.97, 118.15) * mm, "mid": v(1852.6, 138.85) * mm, "end": v(1833.5, 126.53) * mm});
            skArc(sketch, "E326", {"start": v(1805.7, 33.07) * mm, "mid": v(1814.96, 12.32) * mm, "end": v(1834.12, 24.53) * mm});
            skArc(sketch, "E327.trimOffspring", {"start": v(1834.12, 24.53) * mm, "mid": v(1882.84, 60.99) * mm, "end": v(1861.97, 118.15) * mm});
            skLineSegment(sketch, "E328", {"start": v(700, 311.33) * mm, "end": v(1902, 311.33) * mm, "construction": true});
            skLineSegment(sketch, "E329", {"start": v(700, 190.67) * mm, "end": v(1902, 190.67) * mm, "construction": true});
            skLineSegment(sketch, "E330", {"start": v(52.76, 67.43) * mm, "end": v(1902, 73.1) * mm, "construction": true});
            skLineSegment(sketch, "E331", {"start": v(770.07, 69.63) * mm, "end": v(769.97, 432) * mm, "construction": true});
            skArc(sketch, "E332", {"start": v(768.23, 477.97) * mm, "mid": v(725.9, 445.11) * mm, "end": v(743.4, 394.47) * mm});
            skArc(sketch, "E333", {"start": v(796.6, 469.53) * mm, "mid": v(787.4, 490.47) * mm, "end": v(768.23, 477.97) * mm});
            skArc(sketch, "E334", {"start": v(743.4, 394.47) * mm, "mid": v(752.6, 373.53) * mm, "end": v(771.77, 386.03) * mm});
            skArc(sketch, "E335.trimOffspring", {"start": v(771.77, 386.03) * mm, "mid": v(814.1, 418.89) * mm, "end": v(796.6, 469.53) * mm});
            skLineSegment(sketch, "E336", {"start": v(1470.07, 69.63) * mm, "end": v(1470, 432) * mm, "construction": true});
            skArc(sketch, "E337", {"start": v(1467.99, 483) * mm, "mid": v(1419.41, 446.54) * mm, "end": v(1440.17, 389.46) * mm});
            skArc(sketch, "E338", {"start": v(1496.43, 474.54) * mm, "mid": v(1487.11, 495.26) * mm, "end": v(1467.99, 483) * mm});
            skArc(sketch, "E339", {"start": v(1440.17, 389.46) * mm, "mid": v(1449.48, 368.74) * mm, "end": v(1468.6, 381) * mm});
            skArc(sketch, "E340.trimOffspring", {"start": v(1468.6, 381) * mm, "mid": v(1517.18, 417.46) * mm, "end": v(1496.43, 474.54) * mm});
            skLineSegment(sketch, "E341", {"start": v(951, 432) * mm, "end": v(951, 70) * mm, "construction": true});
            skLineSegment(sketch, "E342", {"start": v(1132, 432) * mm, "end": v(1132.52, 70.74) * mm, "construction": true});
            skLineSegment(sketch, "E343", {"start": v(1470.07, 432) * mm, "end": v(1470.05, 502) * mm, "construction": true});
            skLineSegment(sketch, "E344", {"start": v(1651, 432) * mm, "end": v(1651, 0) * mm, "construction": true});
            skLineSegment(sketch, "E345", {"start": v(1832.52, 432) * mm, "end": v(1833.14, 0) * mm, "construction": true});
            skArc(sketch, "E346", {"start": v(1650.7, 483) * mm, "mid": v(1602.12, 446.54) * mm, "end": v(1622.87, 389.46) * mm});
            skArc(sketch, "E347", {"start": v(1679.13, 474.54) * mm, "mid": v(1669.82, 495.26) * mm, "end": v(1650.7, 483) * mm});
            skArc(sketch, "E348", {"start": v(1622.87, 389.46) * mm, "mid": v(1632.18, 368.74) * mm, "end": v(1651.3, 381) * mm});
            skArc(sketch, "E349.trimOffspring", {"start": v(1651.3, 381) * mm, "mid": v(1699.88, 417.46) * mm, "end": v(1679.13, 474.54) * mm});
            skArc(sketch, "E350", {"start": v(1830.3, 483) * mm, "mid": v(1781.74, 446.54) * mm, "end": v(1802.49, 389.46) * mm});
            skArc(sketch, "E351", {"start": v(1858.75, 474.54) * mm, "mid": v(1849.44, 495.26) * mm, "end": v(1830.3, 483) * mm});
            skArc(sketch, "E352", {"start": v(1802.49, 389.46) * mm, "mid": v(1811.8, 368.74) * mm, "end": v(1830.93, 381) * mm});
            skArc(sketch, "E353.trimOffspring", {"start": v(1830.93, 381) * mm, "mid": v(1879.5, 417.46) * mm, "end": v(1858.75, 474.54) * mm});
            skArc(sketch, "E354", {"start": v(1470.22, 122.78) * mm, "mid": v(1421.65, 86.32) * mm, "end": v(1442.4, 29.24) * mm});
            skArc(sketch, "E355", {"start": v(1498.66, 114.32) * mm, "mid": v(1489.35, 135.04) * mm, "end": v(1470.22, 122.78) * mm});
            skArc(sketch, "E356", {"start": v(1442.4, 29.24) * mm, "mid": v(1451.71, 8.52) * mm, "end": v(1470.84, 20.78) * mm});
            skArc(sketch, "E357.trimOffspring", {"start": v(1470.84, 20.78) * mm, "mid": v(1519.42, 57.24) * mm, "end": v(1498.66, 114.32) * mm});
            skArc(sketch, "E358", {"start": v(1650.7, 302.02) * mm, "mid": v(1602.12, 265.56) * mm, "end": v(1622.87, 208.48) * mm});
            skArc(sketch, "E359", {"start": v(1679.13, 293.56) * mm, "mid": v(1669.82, 314.28) * mm, "end": v(1650.7, 302.02) * mm});
            skArc(sketch, "E360", {"start": v(1622.87, 208.48) * mm, "mid": v(1632.18, 187.76) * mm, "end": v(1651.3, 200.02) * mm});
            skArc(sketch, "E361.trimOffspring", {"start": v(1651.3, 200.02) * mm, "mid": v(1699.88, 236.48) * mm, "end": v(1679.13, 293.56) * mm});
            skArc(sketch, "E362", {"start": v(1469.72, 302.02) * mm, "mid": v(1421.15, 265.56) * mm, "end": v(1441.9, 208.48) * mm});
            skArc(sketch, "E363", {"start": v(1498.17, 293.56) * mm, "mid": v(1488.85, 314.28) * mm, "end": v(1469.72, 302.02) * mm});
            skArc(sketch, "E364", {"start": v(1441.9, 208.48) * mm, "mid": v(1451.22, 187.76) * mm, "end": v(1470.34, 200.02) * mm});
            skArc(sketch, "E365.trimOffspring", {"start": v(1470.34, 200.02) * mm, "mid": v(1518.92, 236.48) * mm, "end": v(1498.17, 293.56) * mm});
            skArc(sketch, "E366", {"start": v(1832.46, 302.02) * mm, "mid": v(1783.89, 265.56) * mm, "end": v(1804.64, 208.48) * mm});
            skArc(sketch, "E367", {"start": v(1860.9, 293.56) * mm, "mid": v(1851.59, 314.28) * mm, "end": v(1832.46, 302.02) * mm});
            skArc(sketch, "E368", {"start": v(1804.64, 208.48) * mm, "mid": v(1813.95, 187.76) * mm, "end": v(1833.08, 200.02) * mm});
            skArc(sketch, "E369.trimOffspring", {"start": v(1833.08, 200.02) * mm, "mid": v(1881.65, 236.48) * mm, "end": v(1860.9, 293.56) * mm});
            skLineSegment(sketch, "E370", {"start": v(1041.5, 130.33) * mm, "end": v(1041.53, 365.69) * mm, "construction": true});
            skLineSegment(sketch, "E371", {"start": v(769.99, 365.69) * mm, "end": v(951, 365.69) * mm, "construction": true});
            skArc(sketch, "E372", {"start": v(867.11, 411.42) * mm, "mid": v(819.12, 382) * mm, "end": v(835.52, 328.16) * mm});
            skArc(sketch, "E373", {"start": v(893.94, 398.91) * mm, "mid": v(887.9, 420.98) * mm, "end": v(867.11, 411.42) * mm});
            skArc(sketch, "E374", {"start": v(835.52, 328.16) * mm, "mid": v(844.73, 307.22) * mm, "end": v(863.9, 319.72) * mm});
            skArc(sketch, "E375.trimOffspring", {"start": v(863.9, 319.72) * mm, "mid": v(905.13, 349.37) * mm, "end": v(893.94, 398.91) * mm});
            skArc(sketch, "E376", {"start": v(867.11, 290.75) * mm, "mid": v(819.12, 261.34) * mm, "end": v(835.52, 207.5) * mm});
            skArc(sketch, "E377", {"start": v(893.94, 278.25) * mm, "mid": v(887.9, 300.3) * mm, "end": v(867.11, 290.75) * mm});
            skArc(sketch, "E378", {"start": v(835.52, 207.5) * mm, "mid": v(844.73, 186.55) * mm, "end": v(863.9, 199.06) * mm});
            skArc(sketch, "E379.trimOffspring", {"start": v(863.9, 199.06) * mm, "mid": v(905.13, 228.7) * mm, "end": v(893.94, 278.25) * mm});
            skArc(sketch, "E380", {"start": v(867.08, 176.06) * mm, "mid": v(819.08, 146.65) * mm, "end": v(835.5, 92.8) * mm});
            skArc(sketch, "E381", {"start": v(893.9, 163.56) * mm, "mid": v(887.86, 185.62) * mm, "end": v(867.08, 176.06) * mm});
            skArc(sketch, "E382", {"start": v(835.5, 92.8) * mm, "mid": v(844.7, 71.87) * mm, "end": v(863.86, 84.37) * mm});
            skArc(sketch, "E383.trimOffspring", {"start": v(863.86, 84.37) * mm, "mid": v(905.1, 114.01) * mm, "end": v(893.9, 163.56) * mm});
            skLineSegment(sketch, "E384", {"start": v(862.1, 130.33) * mm, "end": v(862.13, 365.69) * mm, "construction": true});
            skLineSegment(sketch, "E385", {"start": v(1470.07, 432) * mm, "end": v(1651, 432) * mm, "construction": true});
            skLineSegment(sketch, "E386", {"start": v(1651, 432) * mm, "end": v(1832.52, 432) * mm, "construction": true});
            skLineSegment(sketch, "E387", {"start": v(1560.8, 341.8) * mm, "end": v(1561.36, 162) * mm, "construction": true});
            skLineSegment(sketch, "E388", {"start": v(1561.64, 72.06) * mm, "end": v(1741.76, 72.61) * mm, "construction": true});
            skPoint(sketch, "E388.endSnap0", {"position": v(1741.76, 432) * mm});
            skLineSegment(sketch, "E389", {"start": v(1741.76, 162.1) * mm, "end": v(1741.76, 341.63) * mm, "construction": true});
            skLineSegment(sketch, "E390", {"start": v(1470.03, 251.02) * mm, "end": v(1652.43, 74.8) * mm, "construction": true});
            skLineSegment(sketch, "E391", {"start": v(1651, 251.02) * mm, "end": v(1470.53, 71.78) * mm, "construction": true});
            skLineSegment(sketch, "E392", {"start": v(1651, 432) * mm, "end": v(1832.77, 251.02) * mm, "construction": true});
            skLineSegment(sketch, "E393", {"start": v(1651, 432) * mm, "end": v(1470.03, 251.02) * mm, "construction": true});
            skLineSegment(sketch, "E394", {"start": v(1470.07, 432) * mm, "end": v(1651, 251.02) * mm, "construction": true});
            skLineSegment(sketch, "E395", {"start": v(1832.77, 251.02) * mm, "end": v(1652.43, 74.8) * mm, "construction": true});
            skLineSegment(sketch, "E396", {"start": v(1651, 251.02) * mm, "end": v(1833.96, 75.53) * mm, "construction": true});
            skLineSegment(sketch, "E397", {"start": v(1651, 251.02) * mm, "end": v(1832.52, 432) * mm, "construction": true});
            skPoint(sketch, "E398.orphan", {"position": v(1560.53, 432) * mm});
            skArc(sketch, "E399", {"start": v(1560.5, 392.8) * mm, "mid": v(1511.93, 356.34) * mm, "end": v(1532.68, 299.27) * mm});
            skArc(sketch, "E400", {"start": v(1588.94, 384.34) * mm, "mid": v(1579.63, 405.06) * mm, "end": v(1560.5, 392.8) * mm});
            skArc(sketch, "E401", {"start": v(1532.68, 299.27) * mm, "mid": v(1542, 278.54) * mm, "end": v(1561.12, 290.8) * mm});
            skArc(sketch, "E402.trimOffspring", {"start": v(1561.12, 290.8) * mm, "mid": v(1609.7, 327.26) * mm, "end": v(1588.94, 384.34) * mm});
            skArc(sketch, "E403", {"start": v(1741.45, 392.63) * mm, "mid": v(1692.88, 356.17) * mm, "end": v(1713.63, 299.1) * mm});
            skArc(sketch, "E404", {"start": v(1769.9, 384.17) * mm, "mid": v(1760.58, 404.9) * mm, "end": v(1741.45, 392.63) * mm});
            skArc(sketch, "E405", {"start": v(1713.63, 299.1) * mm, "mid": v(1722.94, 278.37) * mm, "end": v(1742.07, 290.63) * mm});
            skArc(sketch, "E406.trimOffspring", {"start": v(1742.07, 290.63) * mm, "mid": v(1790.64, 327.1) * mm, "end": v(1769.9, 384.17) * mm});
            skArc(sketch, "E407", {"start": v(1560.25, 214.56) * mm, "mid": v(1511.67, 178.1) * mm, "end": v(1532.42, 121.02) * mm});
            skArc(sketch, "E408", {"start": v(1588.69, 206.1) * mm, "mid": v(1579.37, 226.82) * mm, "end": v(1560.25, 214.56) * mm});
            skArc(sketch, "E409", {"start": v(1532.42, 121.02) * mm, "mid": v(1541.74, 100.3) * mm, "end": v(1560.87, 112.56) * mm});
            skArc(sketch, "E410.trimOffspring", {"start": v(1560.87, 112.56) * mm, "mid": v(1609.44, 149.02) * mm, "end": v(1588.69, 206.1) * mm});
            skPoint(sketch, "E411.endSnap0", {"position": v(1742.19, 253.92) * mm});
            skArc(sketch, "E412", {"start": v(1741.88, 214.56) * mm, "mid": v(1693.3, 178.1) * mm, "end": v(1714.05, 121.02) * mm});
            skArc(sketch, "E413", {"start": v(1770.32, 206.1) * mm, "mid": v(1761, 226.82) * mm, "end": v(1741.88, 214.56) * mm});
            skArc(sketch, "E414", {"start": v(1714.05, 121.02) * mm, "mid": v(1723.37, 100.3) * mm, "end": v(1742.5, 112.56) * mm});
            skArc(sketch, "E415.trimOffspring", {"start": v(1742.5, 112.56) * mm, "mid": v(1791.07, 149.02) * mm, "end": v(1770.32, 206.1) * mm});
            skArc(sketch, "E416.MirrorCS", {"start": v(1700.97, 582) * mm, "mid": v(1708.04, 579.07) * mm, "end": v(1710.97, 572) * mm});
            skArc(sketch, "E417.MirrorCS", {"start": v(1590.97, 572) * mm, "mid": v(1593.9, 579.07) * mm, "end": v(1600.97, 582) * mm});
            skArc(sketch, "E418.MirrorCS", {"start": v(1613.53, 519.44) * mm, "mid": v(1606.46, 522.37) * mm, "end": v(1603.53, 529.44) * mm});
            skLineSegment(sketch, "E419.MirrorCS", {"start": v(1603.53, 537) * mm, "end": v(1603.53, 529.44) * mm});
            skLineSegment(sketch, "E420.MirrorCS", {"start": v(1698.4, 537) * mm, "end": v(1698.4, 529.44) * mm});
            skLineSegment(sketch, "E421.MirrorCS", {"start": v(1710.97, 572) * mm, "end": v(1710.97, 502) * mm});
            skArc(sketch, "E422.MirrorCS", {"start": v(1698.4, 529.44) * mm, "mid": v(1695.48, 522.37) * mm, "end": v(1688.4, 519.44) * mm});
            skLineSegment(sketch, "E423.MirrorCS", {"start": v(1668.4, 567) * mm, "end": v(1633.53, 567) * mm});
            skLineSegment(sketch, "E424.MirrorCS", {"start": v(1650.97, 582) * mm, "end": v(1600.97, 582) * mm});
            skLineSegment(sketch, "E425.MirrorCS", {"start": v(1650.97, 582) * mm, "end": v(1700.97, 582) * mm});
            skPoint(sketch, "E426.MirrorP", {"position": v(1698.4, 567) * mm});
            skLineSegment(sketch, "E427.MirrorCS", {"start": v(1613.53, 519.44) * mm, "end": v(1688.4, 519.44) * mm});
            skPoint(sketch, "E428.MirrorP", {"position": v(1603.53, 567) * mm});
            skPoint(sketch, "E429.MirrorP", {"position": v(1603.53, 519.44) * mm});
            skPoint(sketch, "E430.MirrorP", {"position": v(1698.4, 519.44) * mm});
            skPoint(sketch, "E431.MirrorP", {"position": v(1710.97, 582) * mm});
            skPoint(sketch, "E432.MirrorP", {"position": v(1590.97, 582) * mm});
            skLineSegment(sketch, "E433", {"start": v(1590.97, 572) * mm, "end": v(1590.97, 502) * mm});
            skLineSegment(sketch, "E434.trimOffspring", {"start": v(891, 502) * mm, "end": v(705, 502) * mm});
            skLineSegment(sketch, "E435", {"start": v(700, 251) * mm, "end": v(1202, 251) * mm, "construction": true});
            skArc(sketch, "E436.MirrorCS", {"start": v(1700.97, -80) * mm, "mid": v(1708.04, -77.07) * mm, "end": v(1710.97, -70) * mm});
            skArc(sketch, "E437.MirrorCS", {"start": v(1613.53, -17.44) * mm, "mid": v(1606.46, -20.37) * mm, "end": v(1603.53, -27.44) * mm});
            skArc(sketch, "E438.MirrorCS", {"start": v(1698.4, -27.44) * mm, "mid": v(1695.48, -20.37) * mm, "end": v(1688.4, -17.44) * mm});
            skArc(sketch, "E439.MirrorCS", {"start": v(1591, -70) * mm, "mid": v(1593.93, -77.07) * mm, "end": v(1601, -80) * mm});
            skPoint(sketch, "E440.MirrorP", {"position": v(1698.4, -17.44) * mm});
            skPoint(sketch, "E441.MirrorP", {"position": v(1590.97, -80) * mm});
            skLineSegment(sketch, "E442.MirrorCS", {"start": v(1651, -80) * mm, "end": v(1601, -80) * mm});
            skPoint(sketch, "E443.MirrorP", {"position": v(1710.97, -80) * mm});
            skLineSegment(sketch, "E444.MirrorCS", {"start": v(1613.53, -17.44) * mm, "end": v(1688.4, -17.44) * mm});
            skLineSegment(sketch, "E445.MirrorCS", {"start": v(1650.97, -80) * mm, "end": v(1700.97, -80) * mm});
            skLineSegment(sketch, "E446.MirrorCS", {"start": v(1668.4, -65) * mm, "end": v(1633.53, -65) * mm});
            skLineSegment(sketch, "E447.MirrorCS", {"start": v(1591, -70) * mm, "end": v(1591, 0) * mm});
            skLineSegment(sketch, "E448.MirrorCS", {"start": v(1710.97, -70) * mm, "end": v(1710.97, 0) * mm});
            skLineSegment(sketch, "E449.MirrorCS", {"start": v(1698.4, -35) * mm, "end": v(1698.4, -27.44) * mm});
            skPoint(sketch, "E450.MirrorP", {"position": v(1603.53, -17.44) * mm});
            skLineSegment(sketch, "E451.MirrorCS", {"start": v(1603.53, -35) * mm, "end": v(1603.53, -27.44) * mm});
            skLineSegment(sketch, "E452.trimOffspring", {"start": v(1011, 0) * mm, "end": v(1197, 0) * mm, "construction": true});
            skLineSegment(sketch, "E453.trimOffspring", {"start": v(1011, 0) * mm, "end": v(1202, 0) * mm});
            skLineSegment(sketch, "E454", {"start": v(1651, 502) * mm, "end": v(1651, 612.07) * mm, "construction": true});
            skLineSegment(sketch, "E455.trimOffspring", {"start": v(1590.97, 502) * mm, "end": v(1400, 502) * mm});
            skLineSegment(sketch, "E456", {"start": v(1710.97, 502) * mm, "end": v(1897, 502) * mm});
            skLineSegment(sketch, "E457.trimOffspring", {"start": v(1710.97, 0) * mm, "end": v(1897, 0) * mm, "construction": true});
            skLineSegment(sketch, "E458.trimOffspring", {"start": v(1710.97, 0) * mm, "end": v(1902, 0) * mm});
            skLineSegment(sketch, "E459", {"start": v(1405, 0) * mm, "end": v(1591, 0) * mm});
            skArc(sketch, "E460.MirrorCS", {"start": v(1001, 582) * mm, "mid": v(1008.07, 579.07) * mm, "end": v(1011, 572) * mm});
            skArc(sketch, "E461.MirrorCS", {"start": v(891, 572) * mm, "mid": v(893.93, 579.07) * mm, "end": v(901, 582) * mm});
            skArc(sketch, "E462.MirrorCS", {"start": v(913.56, 519.44) * mm, "mid": v(906.5, 522.37) * mm, "end": v(903.56, 529.44) * mm});
            skLineSegment(sketch, "E463.MirrorCS", {"start": v(903.56, 537) * mm, "end": v(903.56, 529.44) * mm});
            skLineSegment(sketch, "E464.MirrorCS", {"start": v(998.44, 537) * mm, "end": v(998.44, 529.44) * mm});
            skLineSegment(sketch, "E465.MirrorCS", {"start": v(1011, 572) * mm, "end": v(1011, 502) * mm});
            skArc(sketch, "E466.MirrorCS", {"start": v(998.44, 529.44) * mm, "mid": v(995.5, 522.37) * mm, "end": v(988.44, 519.44) * mm});
            skLineSegment(sketch, "E467.MirrorCS", {"start": v(968.44, 567) * mm, "end": v(933.56, 567) * mm});
            skLineSegment(sketch, "E468.MirrorCS", {"start": v(951, 582) * mm, "end": v(901, 582) * mm});
            skLineSegment(sketch, "E469.MirrorCS", {"start": v(951, 582) * mm, "end": v(1001, 582) * mm});
            skPoint(sketch, "E470.MirrorP", {"position": v(998.44, 567) * mm});
            skLineSegment(sketch, "E471.MirrorCS", {"start": v(913.56, 519.44) * mm, "end": v(988.44, 519.44) * mm});
            skPoint(sketch, "E472.MirrorP", {"position": v(903.56, 567) * mm});
            skPoint(sketch, "E473.MirrorP", {"position": v(903.56, 519.44) * mm});
            skPoint(sketch, "E474.MirrorP", {"position": v(998.44, 519.44) * mm});
            skPoint(sketch, "E475.MirrorP", {"position": v(1011, 582) * mm});
            skPoint(sketch, "E476.MirrorP", {"position": v(891, 582) * mm});
            skLineSegment(sketch, "E477", {"start": v(891, 572) * mm, "end": v(891, 502) * mm});
            skArc(sketch, "E478.MirrorCS", {"start": v(1001, -80) * mm, "mid": v(1008.07, -77.07) * mm, "end": v(1011, -70) * mm});
            skArc(sketch, "E479.MirrorCS", {"start": v(913.56, -17.44) * mm, "mid": v(906.5, -20.37) * mm, "end": v(903.56, -27.44) * mm});
            skArc(sketch, "E480.MirrorCS", {"start": v(998.44, -27.44) * mm, "mid": v(995.5, -20.37) * mm, "end": v(988.44, -17.44) * mm});
            skArc(sketch, "E481.MirrorCS", {"start": v(891, -70) * mm, "mid": v(893.93, -77.07) * mm, "end": v(901, -80) * mm});
            skPoint(sketch, "E482.MirrorP", {"position": v(998.44, -17.44) * mm});
            skPoint(sketch, "E483.MirrorP", {"position": v(891, -80) * mm});
            skPoint(sketch, "E484.MirrorP", {"position": v(1011, -80) * mm});
            skPoint(sketch, "E485.MirrorP", {"position": v(903.56, -65) * mm});
            skLineSegment(sketch, "E486.MirrorCS", {"start": v(913.56, -17.44) * mm, "end": v(988.44, -17.44) * mm});
            skPoint(sketch, "E487.MirrorP", {"position": v(998.44, -65) * mm});
            skLineSegment(sketch, "E488.MirrorCS", {"start": v(901, -80) * mm, "end": v(1001, -80) * mm});
            skLineSegment(sketch, "E489.MirrorCS", {"start": v(968.44, -65) * mm, "end": v(933.56, -65) * mm});
            skLineSegment(sketch, "E490.MirrorCS", {"start": v(891, -70) * mm, "end": v(891, 0) * mm});
            skLineSegment(sketch, "E491.MirrorCS", {"start": v(1011, -70) * mm, "end": v(1011, 0) * mm});
            skLineSegment(sketch, "E492.MirrorCS", {"start": v(998.44, -35) * mm, "end": v(998.44, -27.44) * mm});
            skPoint(sketch, "E493.MirrorP", {"position": v(903.56, -17.44) * mm});
            skLineSegment(sketch, "E494.MirrorCS", {"start": v(903.56, -35) * mm, "end": v(903.56, -27.44) * mm});
            skLineSegment(sketch, "E495", {"start": v(951.03, 502) * mm, "end": v(951.03, 612.07) * mm, "construction": true});
            skArc(sketch, "E496.filletArc", {"start": v(903.56, -35) * mm, "mid": v(912.35, -56.21) * mm, "end": v(933.56, -65) * mm});
            skArc(sketch, "E497.filletArc", {"start": v(968.44, -65) * mm, "mid": v(989.65, -56.21) * mm, "end": v(998.44, -35) * mm});
            skArc(sketch, "E498.filletArc", {"start": v(933.56, 567) * mm, "mid": v(912.35, 558.21) * mm, "end": v(903.56, 537) * mm});
            skArc(sketch, "E499.filletArc", {"start": v(998.44, 537) * mm, "mid": v(989.65, 558.21) * mm, "end": v(968.44, 567) * mm});
            skArc(sketch, "E500.filletArc", {"start": v(1633.53, 567) * mm, "mid": v(1612.32, 558.21) * mm, "end": v(1603.53, 537) * mm});
            skArc(sketch, "E501.filletArc", {"start": v(1698.4, 537) * mm, "mid": v(1689.62, 558.21) * mm, "end": v(1668.4, 567) * mm});
            skArc(sketch, "E502.filletArc", {"start": v(1603.53, -35) * mm, "mid": v(1612.32, -56.21) * mm, "end": v(1633.53, -65) * mm});
            skArc(sketch, "E503.filletArc", {"start": v(1668.4, -65) * mm, "mid": v(1689.62, -56.21) * mm, "end": v(1698.4, -35) * mm});
            skLineSegment(sketch, "E504", {"start": v(1405, 502) * mm, "end": v(1560.5, 502) * mm, "construction": true});
            skLineSegment(sketch, "E505", {"start": v(1560.5, 502) * mm, "end": v(1560.5, 472) * mm, "construction": true});
            skCircle(sketch, "E506", {"center": v(1560.5, 472) * mm, "radius": 7.5 * mm});
            skLineSegment(sketch, "E507", {"start": v(1902, 0) * mm, "end": v(1737.11, 0) * mm, "construction": true});
            skLineSegment(sketch, "E508", {"start": v(1902, 0) * mm, "end": v(1741.5, 0) * mm, "construction": true});
            skLineSegment(sketch, "E509", {"start": v(1741.5, 0) * mm, "end": v(1741.5, 32.5) * mm, "construction": true});
            skCircle(sketch, "E510", {"center": v(1741.5, 32.5) * mm, "radius": 7.5 * mm});
            skLineSegment(sketch, "E511", {"start": v(700, 502) * mm, "end": v(841.2, 502) * mm, "construction": true});
            skLineSegment(sketch, "E512", {"start": v(700, 502) * mm, "end": v(860.5, 502) * mm, "construction": true});
            skLineSegment(sketch, "E513", {"start": v(860.5, 502) * mm, "end": v(860.5, 471.5) * mm, "construction": true});
            skCircle(sketch, "E514", {"center": v(860.5, 471.5) * mm, "radius": 7.5 * mm});
            skLineSegment(sketch, "E515", {"start": v(1202, 0) * mm, "end": v(1041.5, 0) * mm, "construction": true});
            skLineSegment(sketch, "E516", {"start": v(1041.5, 0) * mm, "end": v(1041.5, 32.5) * mm, "construction": true});
            skCircle(sketch, "E517", {"center": v(1041.5, 32.5) * mm, "radius": 7.5 * mm});
            skLineSegment(sketch, "E518", {"start": v(1041.5, 130.33) * mm, "end": v(290.44, 130.44) * mm, "construction": true});
            skPoint(sketch, "E519.visualSharp", {"position": v(1202, 502) * mm});
            skArc(sketch, "E519.filletArc", {"start": v(1202, 497) * mm, "mid": v(1200.54, 500.54) * mm, "end": v(1197, 502) * mm});
            skPoint(sketch, "E520.newPointA", {"position": v(1202, 0) * mm});
            skArc(sketch, "E520.filletArc", {"start": v(1197, 0) * mm, "mid": v(1200.54, 1.46) * mm, "end": v(1202, 5) * mm});
            skPoint(sketch, "E521.visualSharp", {"position": v(700, 0) * mm});
            skArc(sketch, "E521.filletArc", {"start": v(700, 5) * mm, "mid": v(701.46, 1.46) * mm, "end": v(705, 0) * mm});
            skPoint(sketch, "E522.visualSharp", {"position": v(700, 502) * mm});
            skArc(sketch, "E522.filletArc", {"start": v(705, 502) * mm, "mid": v(701.46, 500.54) * mm, "end": v(700, 497) * mm});
            skPoint(sketch, "E523.visualSharp", {"position": v(1400, 502) * mm});
            skArc(sketch, "E523.filletArc", {"start": v(1405, 502) * mm, "mid": v(1401.46, 500.54) * mm, "end": v(1400, 497) * mm});
            skPoint(sketch, "E524.visualSharp", {"position": v(1902, 502) * mm});
            skArc(sketch, "E524.filletArc", {"start": v(1902, 497) * mm, "mid": v(1900.54, 500.54) * mm, "end": v(1897, 502) * mm});
            skPoint(sketch, "E525.visualSharp", {"position": v(1902, 0) * mm});
            skArc(sketch, "E525.filletArc", {"start": v(1897, 0) * mm, "mid": v(1900.54, 1.46) * mm, "end": v(1902, 5) * mm, "construction": true});
            skPoint(sketch, "E526.visualSharp", {"position": v(1400, 0) * mm});
            skArc(sketch, "E526.filletArc", {"start": v(1400, 5) * mm, "mid": v(1401.46, 1.46) * mm, "end": v(1405, 0) * mm});
            skSolve(sketch);
        }
        {
            var Q0;
            Q0=makeQuery(id+"F2.imprint","IMPRINT",FACE,{"disambiguationData":[TD([[makeQuery(id+"F2.imprint","IMPRINT",EDGE,{"derivedFrom":sQuery(id+"F2.wireOp",EDGE,"E257")}),1.0]])]});
            var Q1;
            Q1=makeQuery(id+"F2.imprint","IMPRINT",FACE,{"disambiguationData":[TD([[makeQuery(id+"F2.imprint","IMPRINT",EDGE,{"derivedFrom":sQuery(id+"F2.wireOp",EDGE,"b073b882-489f-464e-bef7-669ffca2ee1a")}),1.0]])]});
            extrude(context, id + "F3", {"entities" : qUnion([Q0, Q1]), "depth" : 6 * mm, "offsetDistance" : 25 * mm});
        }
        {
            var Q0;
            Q0=makeQuery(id+"F2.imprint","IMPRINT",FACE,{"disambiguationData":[TD([[makeQuery(id+"F2.imprint","IMPRINT",EDGE,{"derivedFrom":sQuery(id+"F2.wireOp",EDGE,"E318")}),1.0]])]});
            extrude(context, id + "F4", {"entities" : qUnion([Q0]), "depth" : 6 * mm, "offsetDistance" : 25 * mm});
        }
    });
